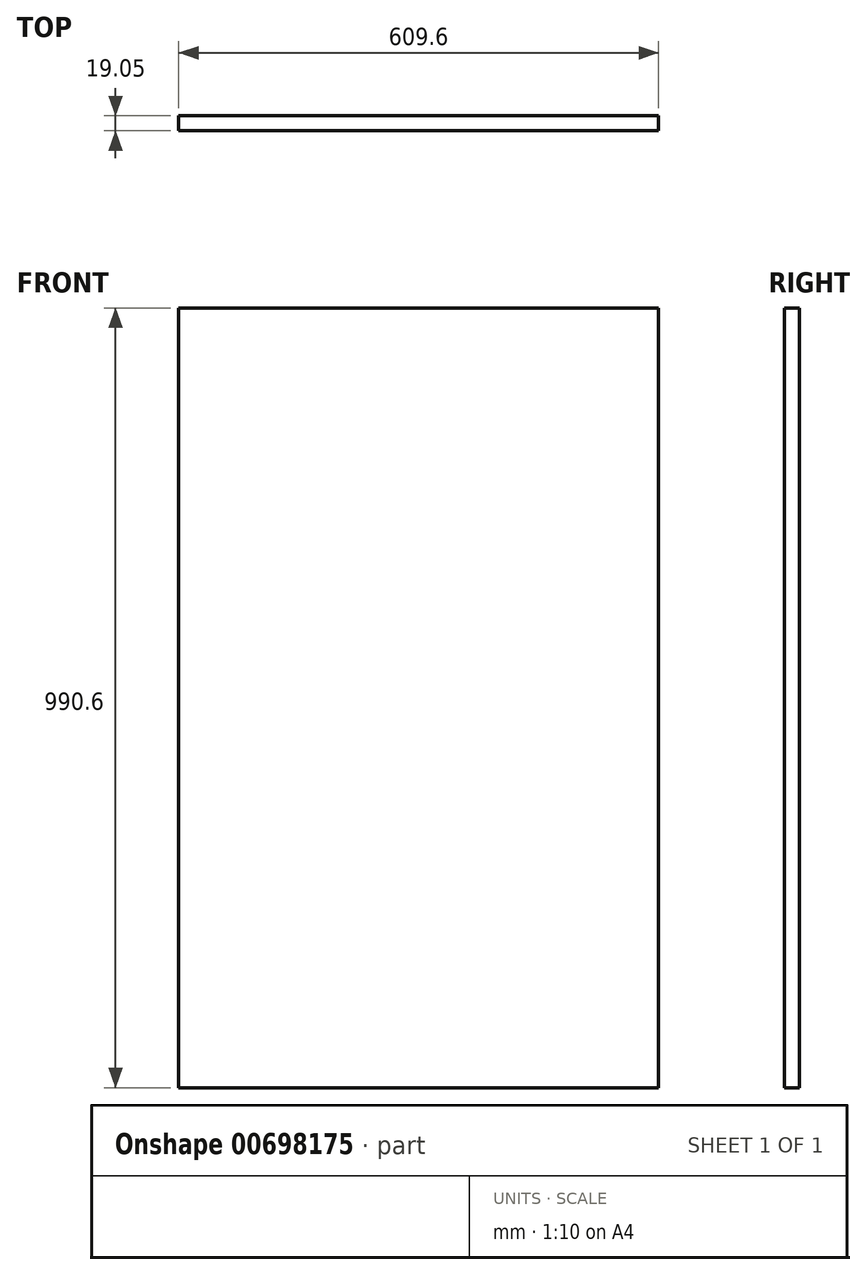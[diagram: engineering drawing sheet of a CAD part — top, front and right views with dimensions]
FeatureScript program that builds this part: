
annotation { "Feature Type Name" : "Feature", "Feature Type Description" : "" }
export const myFeature = defineFeature(function(context is Context, id is Id, definition is map)
    precondition{}
    {
        {
            var Q0;
            Q0=qCreatedBy(makeId("Front.planeOp"),FACE);
            var sketch = newSketch(context, id + "F0", { "sketchPlane" : qUnion([Q0])});
            skLineSegment(sketch, "E0.bottom", {"start": v(304.8, 495.3) * mm, "end": v(-304.8, 495.3) * mm});
            skLineSegment(sketch, "E0.top", {"start": v(304.8, -495.3) * mm, "end": v(-304.8, -495.3) * mm});
            skLineSegment(sketch, "E0.left", {"start": v(304.8, 495.3) * mm, "end": v(304.8, -495.3) * mm});
            skLineSegment(sketch, "E0.right", {"start": v(-304.8, 495.3) * mm, "end": v(-304.8, -495.3) * mm});
            skPoint(sketch, "E0.middle", {"position": v(0, 0) * mm});
            skSolve(sketch);
        }
        {
            var Q0;
            Q0=makeQuery(id+"F0.imprint","IMPRINT",FACE,{"disambiguationData":[TD([[makeQuery(id+"F0.imprint","IMPRINT",EDGE,{"derivedFrom":sQuery(id+"F0.wireOp",EDGE,"E0.bottom")}),1.0]])]});
            extrude(context, id + "F1", {"entities" : qUnion([Q0]), "depth" : 19.05 * mm, "offsetDistance" : 25.4 * mm});
        }
    });
